# Revit family: EL_Teko_Rope_v2
name_source: partatom
category: Osvětlovací tělesa
units: mm (PartAtom-declared; Revit-internal decimal feet)

## family parameters
Bod výpočtu místnosti = Ne
Kóta kruhové spojky = Použít průměr
Název OmniClass = Lighting
Ořezat dutým tvarem při načtení = Ne
Sdílené = Ne
Typ součásti = Normální
Vždy vertikální = Ano
Zachovat orientaci poznámky = Ne
Založené na pracovní rovině = Ne
Zdroj světla = Ano
Číslo OmniClass = 23.80.70.00

## types (39) — shared parameters
Barevný filtr = 16777215
Bodové – úhel paprsku = 30.00°
CE Conformity = CE Mark
Certification = ENEC, ENEC+, EMC, IDA
Control Gear = LED Driver
Diffuser Material  = Flat glass
Délka symbolu zdroje světla = 3048 mm  [stored 10 ft]
EL_Voltage = AC 220V - 240V / 50-60Hz
Emitovat z délky čáry = 610 mm
Housing Height = 191 mm  [stored 0.62664 ft]
Housing Length = 490 mm  [stored 1.60761 ft]
Housing Width = 440 mm  [stored 1.44357 ft]
IK = IK 09 / IK10
IP = IP66
Lampa = LED
Life Time = 120 000 h
Luminaire Material = Kov
Luminaire Type = TEKO R(ope)
Model = TEKO R(ope)
Popis = Street luminaire
Posunu barevné teploty při stmívání lampy = <Žádné>
Terminal Block Poles = 2, 3, 5
URL Luminaire = https://www.el-lumen.cz
URL Manufacturer = https://www.el-lumen.cz
Voltage  = AC 220V - 240V / 50-60Hz
Výchozí výška = 1500 mm  [stored 4.92126 ft]
Výrobce = ELEKTRO-LUMEN, s. r. o.
Weight = 8.7
Úhel bodového pole = 90.00°
Úhel náklonu = 90.00°

## per-type parameters (varying)
| type | CCT | CRI | Luminous Flux of LED | Luminous Flux of Luminaire | Optic | Optical Efficacy | Power |
| TEKO R(ope)  Mxx 10k0 740 | 4000 | 70 | 10000 lm | 8120 lm | M03 | 81.2 | 59 W |
| TEKO R(ope)  Mxx 9k0 740 | 4000 | 70 | 9000 lm | 7308 lm | M03 | 81.2 | 52 W |
| TEKO R(ope)  Mxx 8k0 740 | 4000 | 70 | 8000 lm | 6496 lm | M03 | 81.2 | 45 W |
| TEKO R(ope)  Mxx 7k0 740 | 4000 | 70 | 7000 lm | 5684 lm | M03 | 81.2 | 39 W |
| TEKO R(ope)  Mxx 6k0 740 | 4000 | 70 | 6000 lm | 4872 lm | M03 | 81.2 | 37 W |
| TEKO R(ope)  Mxx 5k0 740 | 4000 | 70 | 5000 lm | 4060 lm | M03 | 81.2 | 31 W |
| TEKO R(ope)  Mxx 4k0 740 | 4000 | 70 | 4000 lm | 3248 lm | M03 | 81.2 | 24 W |
| TEKO R(ope)  Mxx 3k0 740 | 4000 | 70 | 3000 lm | 2436 lm | M03 | 81.2 | 18 W |
| TEKO R(ope)  Mxx 2k0 740 | 4000 | 70 | 2000 lm | 1624 lm | M03 | 81.2 | 12 W |
| TEKO R(ope)  Mxx 9k0 730 | 3000 | 70 | 9000 lm | 7308 lm | M03 | 81.2 | 55 W |
| TEKO R(ope)  Mxx 8k0 730 | 3000 | 70 | 8000 lm | 6496 lm | M03 | 81.2 | 48 W |
| TEKO R(ope)  Mxx 7k0 730 | 3000 | 70 | 7000 lm | 5684 lm | M03 | 81.2 | 42 W |
| TEKO R(ope)  Mxx 6k0 730 | 3000 | 70 | 6000 lm | 4872 lm | M03 | 81.2 | 40 W |
| TEKO R(ope)  Mxx 5k0 730 | 3000 | 70 | 5000 lm | 4060 lm | M03 | 81.2 | 32 W |
| TEKO R(ope)  Mxx 4k0 730 | 3000 | 70 | 4000 lm | 3248 lm | M03 | 81.2 | 25 W |
| TEKO R(ope)  Mxx 3k0 730 | 3000 | 70 | 3000 lm | 2436 lm | M03 | 81.2 | 18 W |
| TEKO R(ope)  Mxx 2k0 730 | 3000 | 70 | 2000 lm | 1624 lm | M03 | 81.2 | 12 W |
| TEKO R(ope)  Mxx 9k0 727 | 2700 | 70 | 9000 lm | 7308 lm | M03 | 81.2 | 59 W |
| TEKO R(ope)  Mxx 8k0 727 | 2700 | 70 | 8000 lm | 6496 lm | M03 | 81.2 | 51 W |
| TEKO R(ope)  Mxx 7k0 727 | 2700 | 70 | 7000 lm | 5684 lm | M03 | 81.2 | 44 W |
| TEKO R(ope)  Mxx 6k0 727 | 2700 | 70 | 6000 lm | 4872 lm | M03 | 81.2 | 43 W |
| TEKO R(ope)  Mxx 5k0 727 | 2700 | 70 | 5000 lm | 4060 lm | M03 | 81.2 | 34 W |
| TEKO R(ope)  Mxx 4k0 727 | 2700 | 70 | 4000 lm | 3248 lm | M03 | 81.2 | 27 W |
| TEKO R(ope)  Mxx 3k0 727 | 2700 | 70 | 3000 lm | 2436 lm | M03 | 81.2 | 20 W |
| TEKO R(ope)  Mxx 2k0 727 | 2700 | 70 | 2000 lm | 1624 lm | M03 | 81.2 | 13 W |
| TEKO R(ope)  Mxx 8k0 722 | 2200 | 70 | 8000 lm | 6496 lm | M03 | 81.2 | 60 W |
| TEKO R(ope)  Mxx 7k0 722 | 2200 | 70 | 7000 lm | 5684 lm | M03 | 81.2 | 51 W |
| TEKO R(ope)  Mxx 6k0 722 | 2200 | 70 | 6000 lm | 4872 lm | M03 | 81.2 | 43 W |
| TEKO R(ope)  Mxx 5k0 722 | 2200 | 70 | 5000 lm | 4060 lm | M03 | 81.2 | 40 W |
| TEKO R(ope)  Mxx 4k0 722 | 2200 | 70 | 4000 lm | 3248 lm | M03 | 81.2 | 31 W |
| TEKO R(ope)  Mxx 3k0 722 | 2200 | 70 | 3000 lm | 2436 lm | M03 | 81.2 | 23 W |
| TEKO R(ope)  Mxx 2k0 722 | 2200 | 70 | 2000 lm | 1624 lm | M03 | 81.2 | 15 W |
| TEKO R(ope)  Lxx 8k0 AMB | 1850 | 50 | 8000 lm | 6364 lm | L03 | 79.55 | 54 W |
| TEKO R(ope)  Lxx 7K0 AMB | 1850 | 50 | 7000 lm | 5569 lm | L03 | 79.55 | 47 W |
| TEKO R(ope)  Lxx 6k0 AMB | 1850 | 50 | 6000 lm | 4773 lm | L03 | 79.55 | 40 W |
| TEKO R(ope)  Lxx 5k0 AMB | 1850 | 50 | 5000 lm | 3978 lm | L03 | 79.55 | 36 W |
| TEKO R(ope)  Lxx 4k0 AMB | 1850 | 50 | 4000 lm | 3182 lm | L03 | 79.55 | 28 W |
| TEKO R(ope)  Lxx 3k0 AMB | 1850 | 50 | 3000 lm | 2387 lm | L03 | 79.55 | 21 W |
| TEKO R(ope)  Lxx 2k0 AMB | 1850 | 50 | 2000 lm | 1591 lm | L03 | 79.55 | 14 W |

note: column(s) folded — value = type name in every type: Luminaire Model

note: [stored X ft] marks values corroborated as IEEE doubles in the binary element streams (Revit-internal decimal feet)
